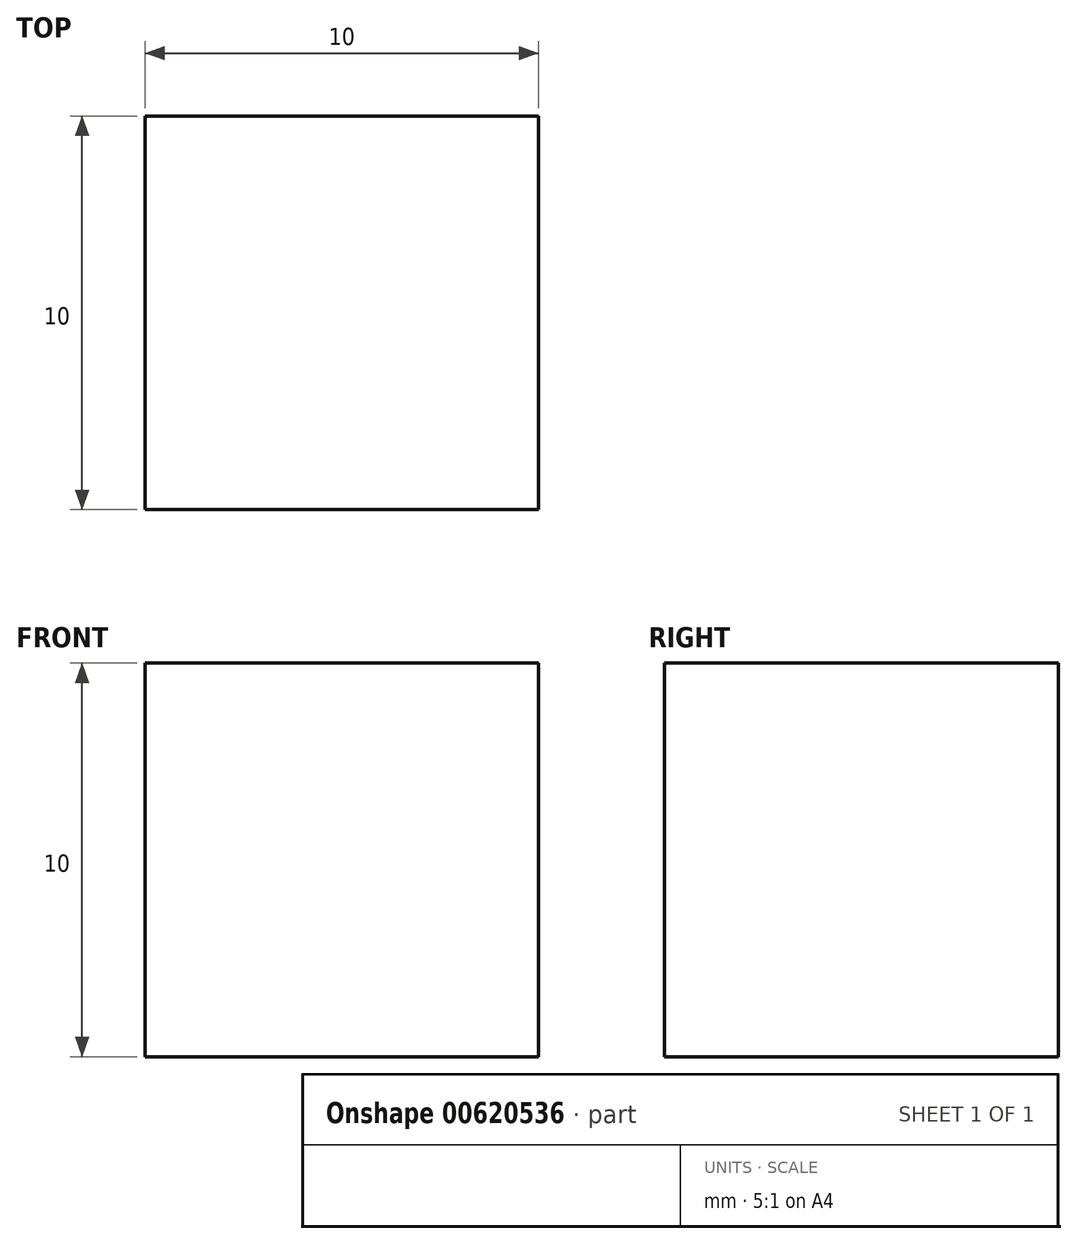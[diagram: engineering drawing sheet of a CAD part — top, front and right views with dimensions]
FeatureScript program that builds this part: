
annotation { "Feature Type Name" : "Feature", "Feature Type Description" : "" }
export const myFeature = defineFeature(function(context is Context, id is Id, definition is map)
    precondition{}
    {
        {
            var Q0;
            Q0=qCreatedBy(makeId("Top.planeOp"),FACE);
            var sketch = newSketch(context, id + "F0", { "sketchPlane" : qUnion([Q0])});
            skLineSegment(sketch, "E0.bottom", {"start": v(5, 5) * mm, "end": v(-5, 5) * mm});
            skLineSegment(sketch, "E0.top", {"start": v(5, -5) * mm, "end": v(-5, -5) * mm});
            skLineSegment(sketch, "E0.left", {"start": v(5, 5) * mm, "end": v(5, -5) * mm});
            skLineSegment(sketch, "E0.right", {"start": v(-5, 5) * mm, "end": v(-5, -5) * mm});
            skPoint(sketch, "E0.middle", {"position": v(0, 0) * mm});
            skSolve(sketch);
        }
        {
            var Q0;
            Q0 = qSketchRegion(id + "F0", true);
            extrude(context, id + "F1", {"entities" : qUnion([Q0]), "depth" : 10 * mm, "offsetDistance" : 25 * mm});
        }
    });
